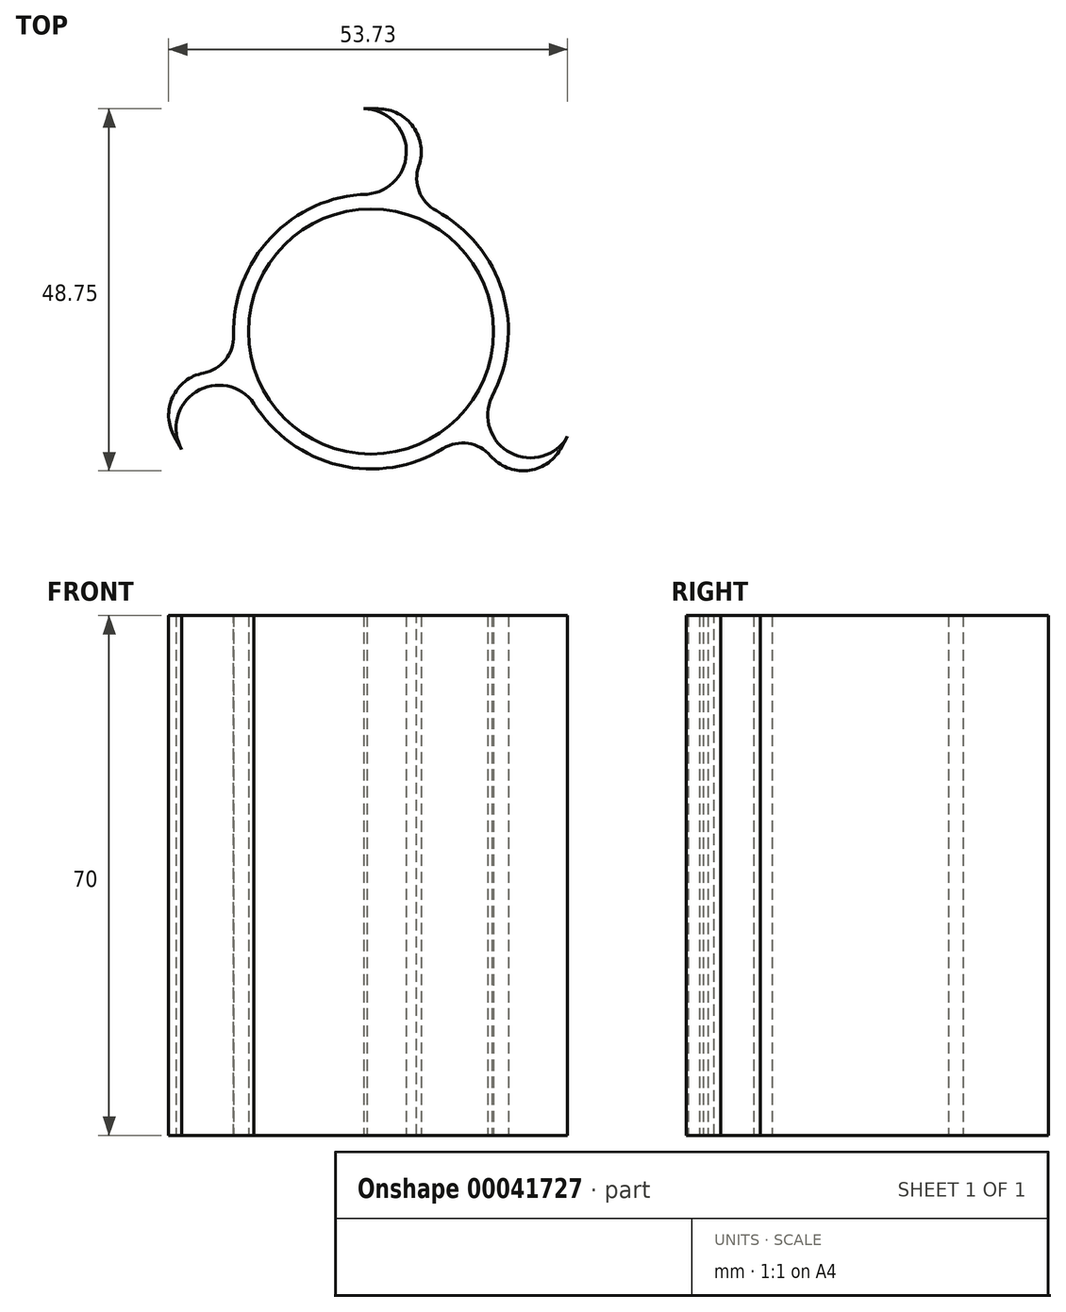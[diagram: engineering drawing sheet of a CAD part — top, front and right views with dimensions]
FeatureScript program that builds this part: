
annotation { "Feature Type Name" : "Feature", "Feature Type Description" : "" }
export const myFeature = defineFeature(function(context is Context, id is Id, definition is map)
    precondition{}
    {
        {
            var Q0;
            Q0=qCreatedBy(makeId("Top.planeOp"),FACE);
            var sketch = newSketch(context, id + "F0", { "sketchPlane" : qUnion([Q0])});
            skCircle(sketch, "E0", {"center": v(0, 0) * mm, "radius": 16.5 * mm});
            skCircle(sketch, "E1", {"center": v(0, 0) * mm, "radius": 18.5 * mm});
            skLineSegment(sketch, "E2", {"start": v(0, 18.5) * mm, "end": v(0, 16.5) * mm, "construction": true});
            skLineSegment(sketch, "E3", {"start": v(0, 0) * mm, "end": v(0, 30) * mm, "construction": true});
            skLineSegment(sketch, "E4", {"start": v(-1, 18.47) * mm, "end": v(1, 18.47) * mm, "construction": true});
            skLineSegment(sketch, "E5", {"start": v(-1, 30) * mm, "end": v(1, 30) * mm});
            skArc(sketch, "E6", {"start": v(1, 18.47) * mm, "mid": v(6.76, 24.24) * mm, "end": v(1, 30) * mm});
            skArc(sketch, "E7", {"start": v(-1, 18.47) * mm, "mid": v(4.76, 24.24) * mm, "end": v(-1, 30) * mm});
            skArc(sketch, "E8.1.0", {"start": v(-16.5, -8.37) * mm, "mid": v(-24.37, -6.26) * mm, "end": v(-26.48, -14.13) * mm});
            skArc(sketch, "E8.1.1", {"start": v(-15.5, -10.1) * mm, "mid": v(-23.37, -8) * mm, "end": v(-25.48, -15.87) * mm});
            skLineSegment(sketch, "E8.1.2", {"start": v(-25.48, -15.87) * mm, "end": v(-26.48, -14.13) * mm});
            skArc(sketch, "E8.2.0", {"start": v(15.5, -10.1) * mm, "mid": v(17.6, -17.98) * mm, "end": v(25.48, -15.87) * mm});
            skArc(sketch, "E8.2.1", {"start": v(16.5, -8.37) * mm, "mid": v(18.6, -16.24) * mm, "end": v(26.48, -14.13) * mm});
            skLineSegment(sketch, "E8.2.2", {"start": v(26.48, -14.13) * mm, "end": v(25.48, -15.87) * mm});
            skSolve(sketch);
        }
        {
            var Q0;
            Q0=qSketchRegion(id+"F0",true);
            extrude(context, id + "F1", {"entities" : qUnion([Q0]), "depth" : 70 * mm});
        }
        {
            var Q0;
            Q0=makeQuery(id+"F1.opExtrude","SWEPT_EDGE",EDGE,{"disambiguationData":[OSD([sQuery(id+"F0.wireOp",EDGE,"E1"),sQuery(id+"F0.wireOp",EDGE,"E6")])]});
            var Q1;
            Q1=makeQuery(id+"F1.opExtrude","SWEPT_EDGE",EDGE,{"disambiguationData":[OSD([sQuery(id+"F0.wireOp",EDGE,"E1"),sQuery(id+"F0.wireOp",EDGE,"E8.2.0")])]});
            var Q2;
            Q2=makeQuery(id+"F1.opExtrude","SWEPT_EDGE",EDGE,{"disambiguationData":[OSD([sQuery(id+"F0.wireOp",EDGE,"E1"),sQuery(id+"F0.wireOp",EDGE,"E8.1.0")])]});
            fillet(context, id + "F2", {"entities" : qUnion([Q0, Q1, Q2]), "radius" : 5 * mm, "tangentPropagation" : true, "allowEdgeOverflow" : false});
        }
    });
